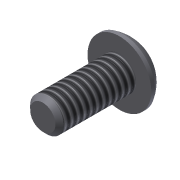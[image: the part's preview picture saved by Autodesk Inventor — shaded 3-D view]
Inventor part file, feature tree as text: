
AUTODESK INVENTOR PART (.ipt)
format: ipt  version: 2013 (Build 170138000, 138)  size: 122,368 bytes
history: native  units: in
note: dims shown in document units (in); Inventor stores cm internally (conversion verified against a paired STEP export)
features: sketch x3, extrude x2, revolve x1, chamfer x1, thread x1
ambient origin geometry x8: Origin, YZ Plane, XZ Plane, XY Plane, X Axis, Y Axis, Z Axis, Center Point
bodies: Solid1 (feature_tree)
feature tree (8):
  extrude  "Extrusion1"  Depth=0.375in TaperAngle=0.0deg
  revolve  "Revolution1"  [1 undecoded]
  extrude  "Extrusion2"  Depth=0.0938in
  chamfer  "Chamfer1"  Distance=0.0625in
  thread  "Thread1"  [1 undecoded]
  sketch  "Sketch1"  dims[d0=0.164in d1=0.375in d2=0.0in]
  sketch  "Sketch2"  dims[d3=0.087in d6=0.08in]
  sketch  "Sketch3"  dims[d7=90.0deg d8=0.0938in d9=0.0625in d10=0.0in d13=0.02in d14=0.125in d15=45.0deg d16=1.0in d17=0.0in d19=0.156in]
note: 2 required parameter values undecoded (feature->parameter linkage not recoverable at this tier; creation-order binding heuristic only, values carry confidence <= 0.55)